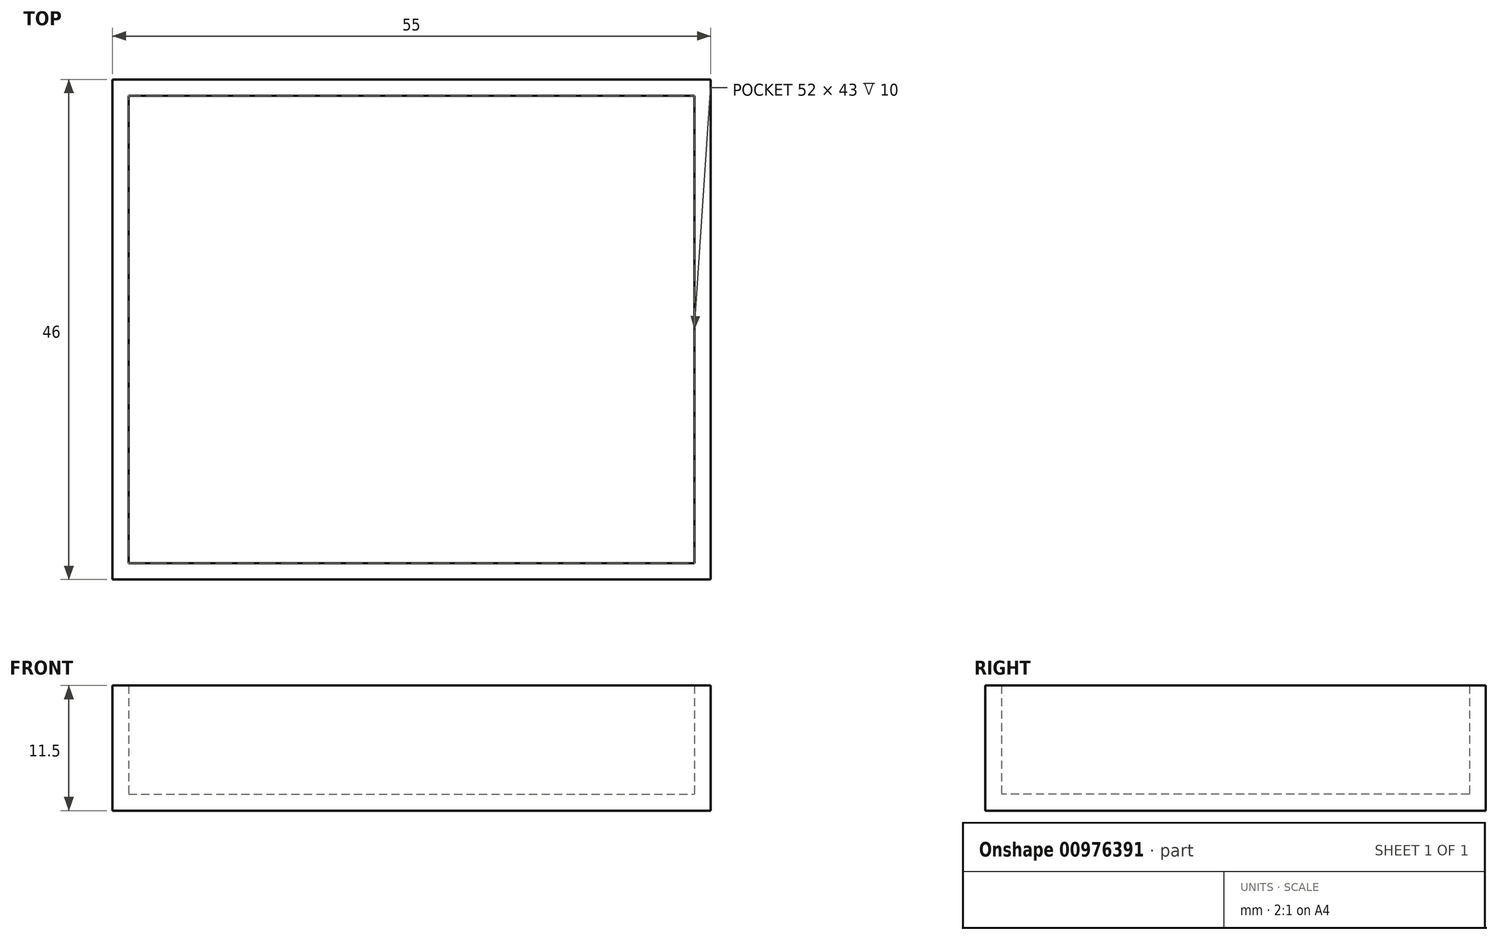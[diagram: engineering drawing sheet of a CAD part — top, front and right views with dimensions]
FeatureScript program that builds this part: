
annotation { "Feature Type Name" : "Feature", "Feature Type Description" : "" }
export const myFeature = defineFeature(function(context is Context, id is Id, definition is map)
    precondition{}
    {
        {
            var Q0;
            Q0=qCreatedBy(makeId("Top.planeOp"),FACE);
            var sketch = newSketch(context, id + "F0", { "sketchPlane" : qUnion([Q0])});
            skLineSegment(sketch, "E0.bottom", {"start": v(-27.5, 23) * mm, "end": v(27.5, 23) * mm});
            skLineSegment(sketch, "E0.top", {"start": v(-27.5, -23) * mm, "end": v(27.5, -23) * mm});
            skLineSegment(sketch, "E0.left", {"start": v(-27.5, 23) * mm, "end": v(-27.5, -23) * mm});
            skLineSegment(sketch, "E0.right", {"start": v(27.5, 23) * mm, "end": v(27.5, -23) * mm});
            skSolve(sketch);
        }
        {
            var Q0;
            Q0 = qSketchRegion(id + "F0", true);
            extrude(context, id + "F1", {"entities" : qUnion([Q0]), "depth" : 1.5 * mm, "offsetDistance" : 25 * mm});
        }
        {
            var Q0;
            Q0=makeQuery(id+"F1.opExtrude","CAP_FACE",FACE,{"disambiguationData":[OSD([sQuery(id+"F0.wireOp",EDGE,"E0.bottom"),sQuery(id+"F0.wireOp",EDGE,"E0.top"),sQuery(id+"F0.wireOp",EDGE,"E0.left"),sQuery(id+"F0.wireOp",EDGE,"E0.right")])],"isStart":false});
            var sketch = newSketch(context, id + "F2", { "sketchPlane" : qUnion([Q0])});
            skLineSegment(sketch, "E1.0", {"start": v(-26, 21.5) * mm, "end": v(26, 21.5) * mm});
            skLineSegment(sketch, "E1.1", {"start": v(-26, 21.5) * mm, "end": v(-26, -21.5) * mm});
            skLineSegment(sketch, "E1.2", {"start": v(-26, -21.5) * mm, "end": v(26, -21.5) * mm});
            skLineSegment(sketch, "E1.3", {"start": v(26, 21.5) * mm, "end": v(26, -21.5) * mm});
            skSolve(sketch);
        }
        {
            var Q0;
            Q0=makeQuery(id+"F2.imprint","IMPRINT",FACE,{"disambiguationData":[TD([[makeQuery(id+"F2.imprint","IMPRINT",EDGE,{"derivedFrom":sQuery(id+"F2.wireOp",EDGE,"E1.0")}),1.0]])]});
            extrude(context, id + "F3", {"entities" : qUnion([Q0]), "operationType" : NewBodyOperationType.ADD, "depth" : 10 * mm, "offsetDistance" : 25 * mm});
        }
    });
